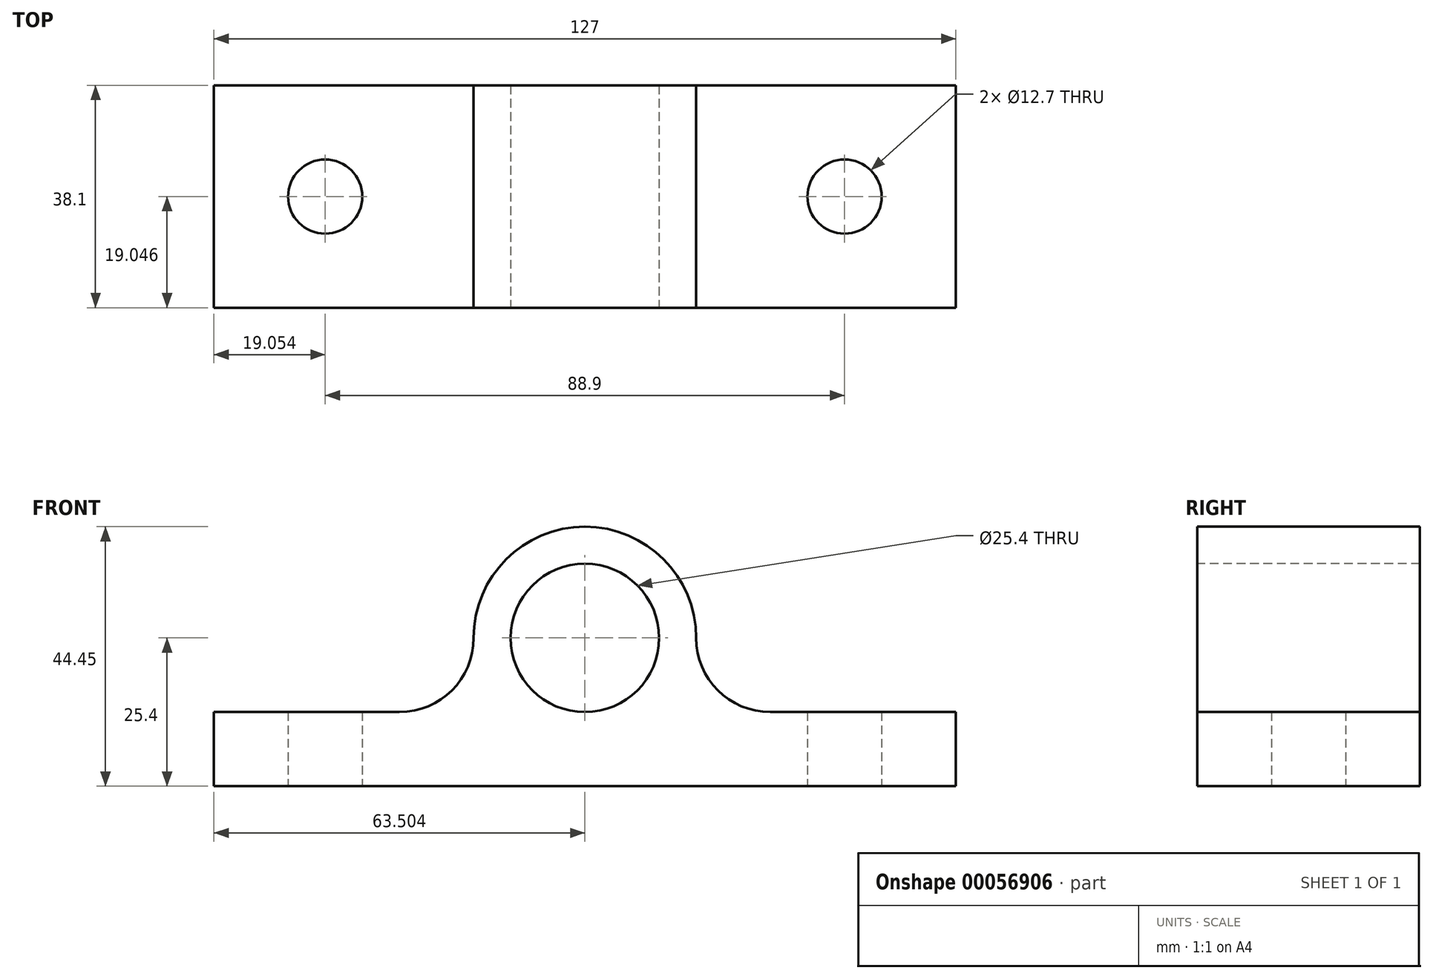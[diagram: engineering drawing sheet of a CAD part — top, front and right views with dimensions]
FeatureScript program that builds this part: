
annotation { "Feature Type Name" : "Feature", "Feature Type Description" : "" }
export const myFeature = defineFeature(function(context is Context, id is Id, definition is map)
    precondition{}
    {
        {
            var Q0;
            Q0=qCreatedBy(makeId("Top.planeOp"),FACE);
            var sketch = newSketch(context, id + "F0", { "sketchPlane" : qUnion([Q0])});
            skLineSegment(sketch, "E0.bottom", {"start": v(-65.6, -6.16) * mm, "end": v(61.4, -6.16) * mm});
            skLineSegment(sketch, "E0.top", {"start": v(-65.6, -44.26) * mm, "end": v(61.4, -44.26) * mm});
            skLineSegment(sketch, "E0.left", {"start": v(-65.6, -6.16) * mm, "end": v(-65.6, -44.26) * mm});
            skLineSegment(sketch, "E0.right", {"start": v(61.4, -6.16) * mm, "end": v(61.4, -44.26) * mm});
            skCircle(sketch, "E1", {"center": v(-46.56, -25.21) * mm, "radius": 6.35 * mm});
            skCircle(sketch, "E2", {"center": v(42.34, -25.21) * mm, "radius": 6.35 * mm});
            skSolve(sketch);
        }
        {
            var Q0;
            Q0=makeQuery(id+"F0.imprint","IMPRINT",FACE,{"disambiguationData":[TD([[makeQuery(id+"F0.imprint","IMPRINT",EDGE,{"derivedFrom":sQuery(id+"F0.wireOp",EDGE,"E0.bottom")}),-1.0]])]});
            extrude(context, id + "F1", {"entities" : qUnion([Q0]), "depth" : 12.7 * mm});
        }
        {
            var Q0;
            Q0=makeQuery(id+"F1.opExtrude","SWEPT_FACE",FACE,{"disambiguationData":[OSD([sQuery(id+"F0.wireOp",EDGE,"E0.top")])]});
            var sketch = newSketch(context, id + "F2", { "sketchPlane" : qUnion([Q0])});
            skCircle(sketch, "E3", {"center": v(-2.1, 25.4) * mm, "radius": 19.05 * mm});
            skLineSegment(sketch, "E4", {"start": v(-65.6, 12.7) * mm, "end": v(61.4, 12.7) * mm});
            skCircle(sketch, "E5", {"center": v(-2.1, 25.4) * mm, "radius": 12.7 * mm});
            skArc(sketch, "E6", {"start": v(-33.86, 12.7) * mm, "mid": v(-24.88, 16.42) * mm, "end": v(-21.16, 25.4) * mm});
            skArc(sketch, "E7", {"start": v(16.94, 25.4) * mm, "mid": v(20.66, 16.42) * mm, "end": v(29.64, 12.7) * mm});
            skSolve(sketch);
        }
        {
            var Q0;
            Q0 = qSketchRegion(id + "F2", true);
            var Q1;
            Q1=makeQuery(id+"F1.opExtrude","SWEPT_FACE",FACE,{"disambiguationData":[OSD([sQuery(id+"F0.wireOp",EDGE,"E0.bottom")])]});
            extrude(context, id + "F3", {"entities" : qUnion([Q0]), "operationType" : NewBodyOperationType.ADD, "endBound" : BoundingType.UP_TO_SURFACE, "oppositeDirection" : true, "endBoundEntityFace" : qUnion([Q1]), "depth" : 25.4 * mm});
        }
    });
